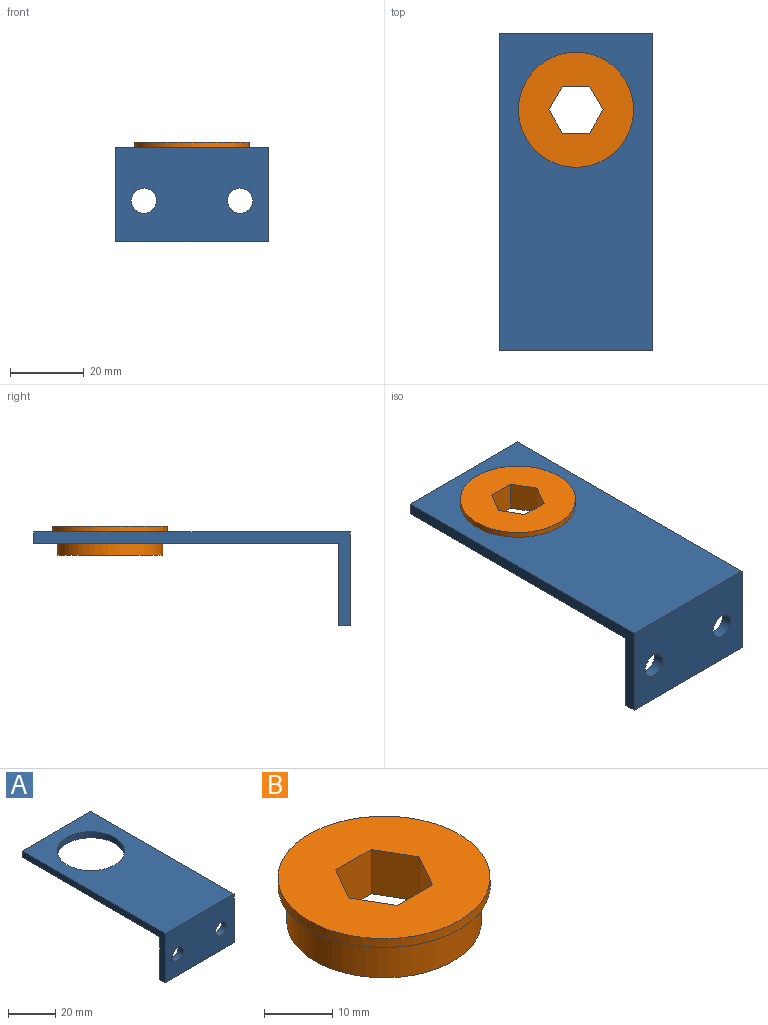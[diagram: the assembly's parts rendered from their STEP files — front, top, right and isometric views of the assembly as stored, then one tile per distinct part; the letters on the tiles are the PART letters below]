
ASSEMBLY  parts=2 mates=1
PART A: 11 faces, bbox 41.3x85.7x25.4 mm
  f0: plane 82.55x41.28mm, normal (0,0,-1), area 2765.9mm2, adj f1,f3,f4,f5,f7
  f1: plane 85.73x25.4mm, normal (-1,0,0), area 342.7mm2, adj f0,f2,f4,f6,f7,f8
  f2: plane 41.28x25.4mm, normal (0,-1,0), area 976.7mm2, adj f1,f3,f6,f8,f9,f10
  f3: plane 85.73x25.4mm, normal (1,0,0), area 342.7mm2, adj f0,f2,f4,f6,f7,f8
  f4: plane 41.28x3.18mm, normal (0,1,0), area 131mm2, adj f0,f1,f3,f6
  f5: cylinder r=14.29mm len=28.58mm, axis (0,0,-1), area 285mm2, adj f0,f6
  f6: plane 85.73x41.28mm, normal (0,0,1), area 2897mm2, adj f1,f2,f3,f4,f5
  f7: plane 41.28x22.23mm, normal (0,1,0), area 845.6mm2, adj f0,f1,f3,f8,f9,f10
  f8: plane 41.28x3.18mm, normal (0,0,-1), area 131mm2, adj f1,f2,f3,f7
  f9: cylinder r=3.38mm len=6.76mm, axis (0,1,0), area 67.4mm2, adj f2,f7
  f10: cylinder r=3.38mm len=6.76mm, axis (0,1,0), area 67.4mm2, adj f2,f7
PART B: 11 faces, bbox 31.1x31.1x7.9 mm
  f0: cylinder r=15.56mm len=31.12mm, axis (0,0,1), area 155.2mm2, adj f1,f2
  f1: plane 31.12x31.12mm, normal (0,0,1), area 620.3mm2, adj f0,f3,f4,f5,f6,f7,f8
  f2: plane 31.12x31.12mm, normal (0,0,-1), area 120.2mm2, adj f0,f9
  f3: plane 7.94x6.36mm, normal (-0.87,-0.5,0), area 58.3mm2, adj f1,f4,f8,f10
  f4: plane 7.94x7.34mm, normal (0,-1,0), area 58.3mm2, adj f1,f3,f5,f10
  f5: plane 7.94x6.36mm, normal (0.87,-0.5,0), area 58.3mm2, adj f1,f4,f6,f10
  f6: plane 7.94x6.36mm, normal (0.87,0.5,0), area 58.3mm2, adj f1,f5,f7,f10
  f7: plane 7.94x7.34mm, normal (0,1,0), area 58.3mm2, adj f1,f6,f8,f10
  f8: plane 7.94x6.36mm, normal (-0.87,0.5,0), area 58.3mm2, adj f1,f3,f7,f10
  f9: cylinder r=14.27mm len=28.55mm, axis (0,0,1), area 569.5mm2, adj f2,f10
  f10: plane 28.55x28.55mm, normal (0,0,-1), area 500mm2, adj f3,f4,f5,f6,f7,f8,f9
PLACE A t=(7.27,-6.86,-6.92)mm
PLACE B t=(-14.59,2.84,-10.1)mm
MATE fastened B.f0 <-> A.f5  axis (0,0,-1) through (-14.59,2.84,-3.75)mm
